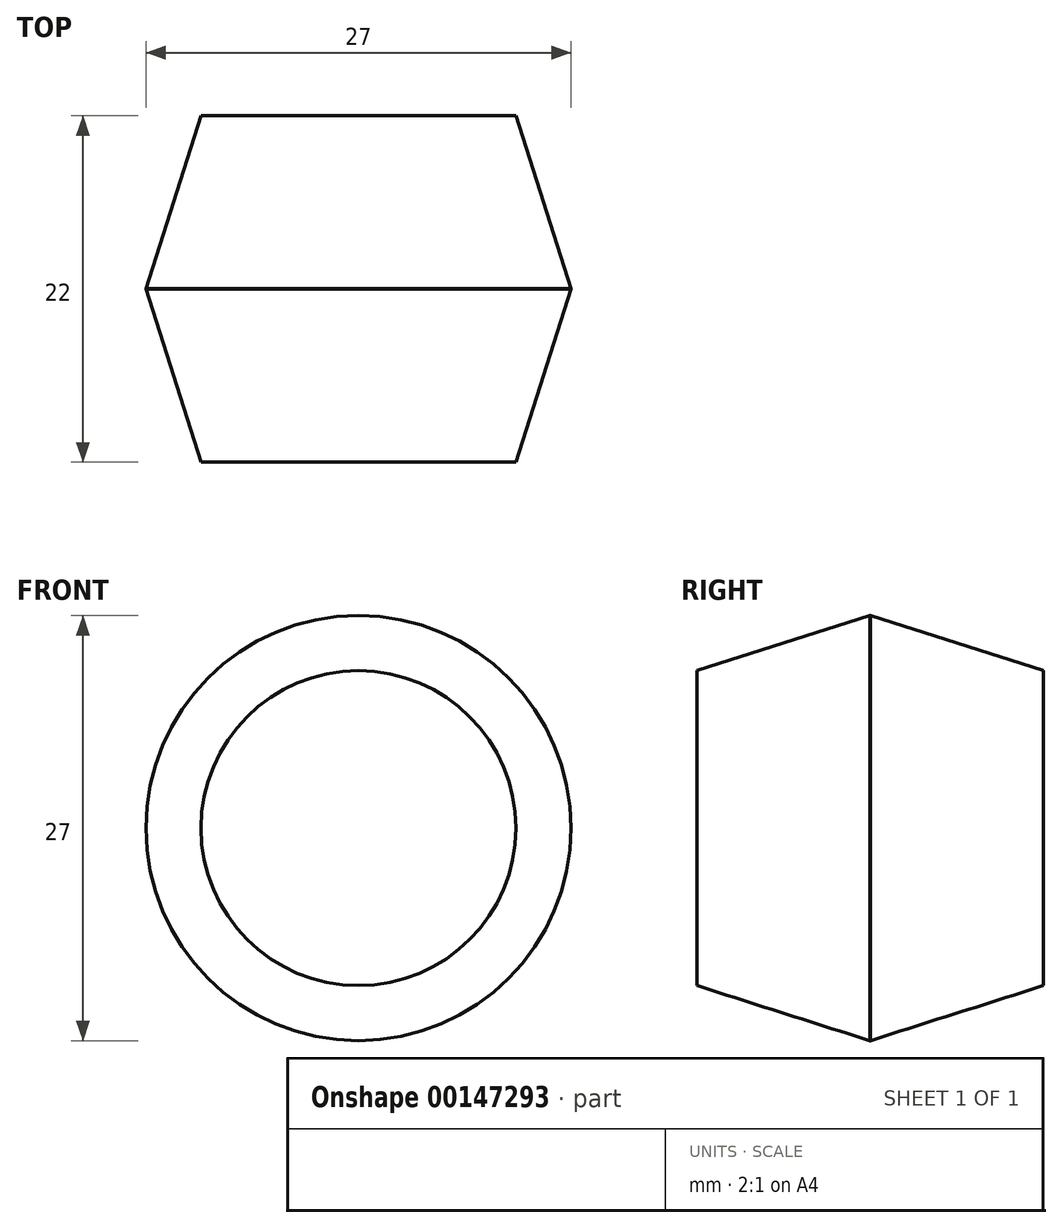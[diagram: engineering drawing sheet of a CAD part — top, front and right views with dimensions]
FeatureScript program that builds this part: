
annotation { "Feature Type Name" : "Feature", "Feature Type Description" : "" }
export const myFeature = defineFeature(function(context is Context, id is Id, definition is map)
    precondition{}
    {
        {
            var Q0;
            Q0=qCreatedBy(makeId("Front.planeOp"),FACE);
            var sketch = newSketch(context, id + "F0", { "sketchPlane" : qUnion([Q0])});
            skCircle(sketch, "E0", {"center": v(0, 0) * mm, "radius": 13.5 * mm});
            skSolve(sketch);
        }
        {
            var Q0;
            Q0=makeQuery(id+"F0.imprint","IMPRINT",FACE,{"disambiguationData":[TD([[makeQuery(id+"F0.imprint","IMPRINT",EDGE,{"derivedFrom":sQuery(id+"F0.wireOp",EDGE,"E0")}),1.0]])]});
            extrude(context, id + "F1", {"entities" : qUnion([Q0]), "depth" : 0.02 * mm});
        }
        {
            var Q0;
            Q0=qCreatedBy(makeId("Front.planeOp"),FACE);
            cPlane(context, id + "F2", {"entities" : qUnion([Q0]), "cplaneType" : CPlaneType.OFFSET, "offset" : 11 * mm, "width" : 152.4 * mm, "height" : 152.4 * mm});
        }
        {
            var Q0;
            Q0=qCreatedBy(id+"F2.planeOp",FACE);
            var sketch = newSketch(context, id + "F3", { "sketchPlane" : qUnion([Q0])});
            skCircle(sketch, "E1", {"center": v(0, 0) * mm, "radius": 10 * mm});
            skSolve(sketch);
        }
        {
            var Q0;
            Q0=makeQuery(id+"F3.imprint","IMPRINT",FACE,{"disambiguationData":[TD([[makeQuery(id+"F3.imprint","IMPRINT",EDGE,{"derivedFrom":sQuery(id+"F3.wireOp",EDGE,"E1")}),1.0]])]});
            var Q1;
            Q1=makeQuery(id+"F1.opExtrude","CAP_FACE",FACE,{"disambiguationData":[OSD([sQuery(id+"F0.wireOp",EDGE,"E0")])],"isStart":false});
            loft(context, id + "F4", {"operationType" : NewBodyOperationType.ADD, "sheetProfilesArray" : [{ "sheetProfileEntities" : qUnion([Q0]) }, { "sheetProfileEntities" : qUnion([Q1]) }]});
        }
        {
            var Q0;
            Q0=makeQuery(id+"F1.opExtrude","SWEPT_BODY",BODY,{"disambiguationData":[OSD([sQuery(id+"F0.wireOp",EDGE,"E0")])]});
            var Q1;
            Q1=qCreatedBy(makeId("Front.planeOp"),FACE);
            mirror(context, id + "F5", {"operationType" : NewBodyOperationType.ADD, "entities" : qUnion([Q0]), "mirrorPlane" : qUnion([Q1])});
        }
    });
